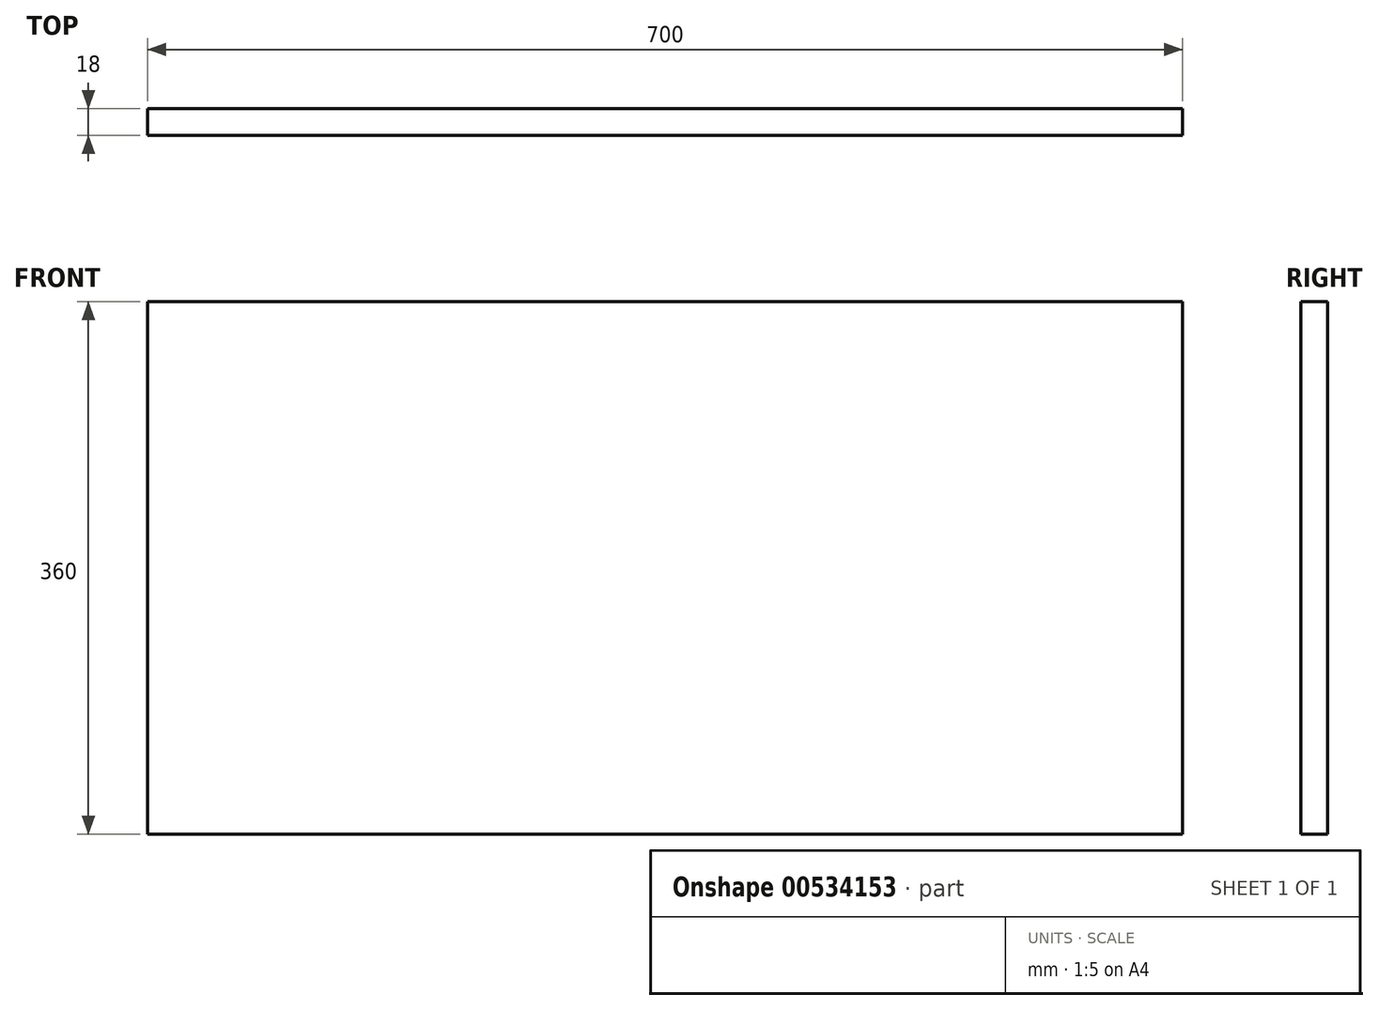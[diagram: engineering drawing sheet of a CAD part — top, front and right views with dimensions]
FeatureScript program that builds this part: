
annotation { "Feature Type Name" : "Feature", "Feature Type Description" : "" }
export const myFeature = defineFeature(function(context is Context, id is Id, definition is map)
    precondition{}
    {
        {
            var Q0;
            Q0=qCreatedBy(makeId("Front.planeOp"),FACE);
            var sketch = newSketch(context, id + "F0", { "sketchPlane" : qUnion([Q0])});
            skLineSegment(sketch, "E0.bottom", {"start": v(0, 0) * mm, "end": v(700, 0) * mm});
            skLineSegment(sketch, "E0.top", {"start": v(0, 360) * mm, "end": v(700, 360) * mm});
            skLineSegment(sketch, "E0.left", {"start": v(0, 0) * mm, "end": v(0, 360) * mm});
            skLineSegment(sketch, "E0.right", {"start": v(700, 0) * mm, "end": v(700, 360) * mm});
            skSolve(sketch);
        }
        {
            var Q0;
            Q0=makeQuery(id+"F0.imprint","IMPRINT",FACE,{"disambiguationData":[TD([[makeQuery(id+"F0.imprint","IMPRINT",EDGE,{"derivedFrom":sQuery(id+"F0.wireOp",EDGE,"E0.bottom")}),1.0]])]});
            extrude(context, id + "F1", {"entities" : qUnion([Q0]), "depth" : 18 * mm, "offsetDistance" : 25 * mm});
        }
    });
